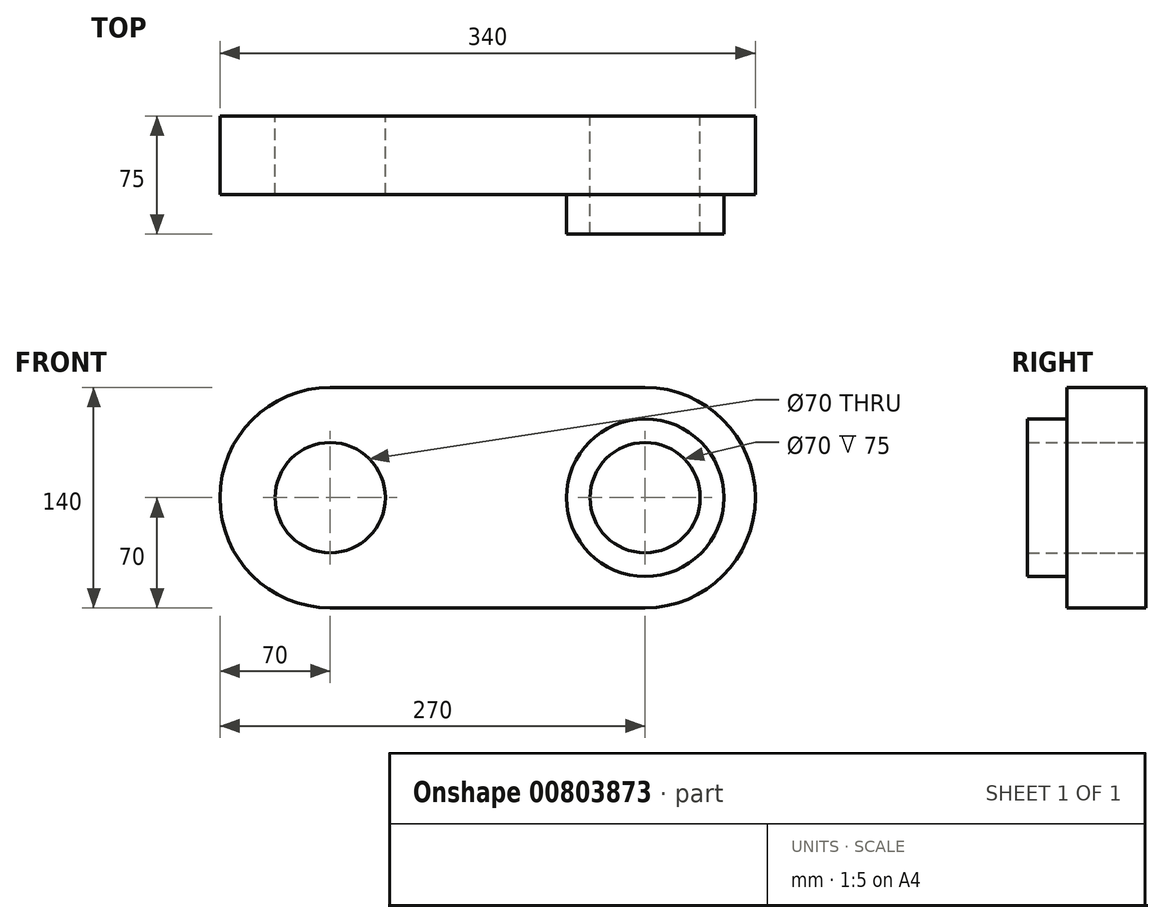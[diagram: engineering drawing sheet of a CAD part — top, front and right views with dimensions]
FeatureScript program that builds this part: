
annotation { "Feature Type Name" : "Feature", "Feature Type Description" : "" }
export const myFeature = defineFeature(function(context is Context, id is Id, definition is map)
    precondition{}
    {
        {
            var Q0;
            Q0=qCreatedBy(makeId("Front.planeOp"),FACE);
            var sketch = newSketch(context, id + "F0", { "sketchPlane" : qUnion([Q0])});
            skLineSegment(sketch, "E0.bottom", {"start": v(-100, 70) * mm, "end": v(100, 70) * mm});
            skLineSegment(sketch, "E0.top", {"start": v(-100, -70) * mm, "end": v(100, -70) * mm});
            skLineSegment(sketch, "E0.left", {"start": v(-100, 70) * mm, "end": v(-100, -70) * mm, "construction": true});
            skLineSegment(sketch, "E0.right", {"start": v(100, 70) * mm, "end": v(100, -70) * mm, "construction": true});
            skLineSegment(sketch, "E1", {"start": v(-100, 0) * mm, "end": v(100, 0) * mm, "construction": true});
            skCircle(sketch, "E2", {"center": v(-100, 0) * mm, "radius": 35 * mm});
            skArc(sketch, "E3", {"start": v(-100, 70) * mm, "mid": v(-170, 0) * mm, "end": v(-100, -70) * mm});
            skCircle(sketch, "E4", {"center": v(100, 0) * mm, "radius": 35 * mm});
            skArc(sketch, "E5", {"start": v(100, -70) * mm, "mid": v(170, 0) * mm, "end": v(100, 70) * mm});
            skSolve(sketch);
        }
        {
            var Q0;
            Q0=makeQuery(id+"F0.imprint","IMPRINT",FACE,{"disambiguationData":[TD([[makeQuery(id+"F0.imprint","IMPRINT",EDGE,{"derivedFrom":sQuery(id+"F0.wireOp",EDGE,"E0.bottom")}),-1.0]])]});
            extrude(context, id + "F1", {"entities" : qUnion([Q0]), "endBound" : BoundingType.SYMMETRIC, "depth" : 50 * mm, "offsetDistance" : 25 * mm});
        }
        {
            var Q0;
            Q0=makeQuery(id+"F1.opExtrude","CAP_FACE",FACE,{"disambiguationData":[OSD([sQuery(id+"F0.wireOp",EDGE,"E0.bottom"),sQuery(id+"F0.wireOp",EDGE,"E0.top"),sQuery(id+"F0.wireOp",EDGE,"E2"),sQuery(id+"F0.wireOp",EDGE,"E3"),sQuery(id+"F0.wireOp",EDGE,"E4"),sQuery(id+"F0.wireOp",EDGE,"E5")])],"isStart":false});
            var sketch = newSketch(context, id + "F2", { "sketchPlane" : qUnion([Q0])});
            skCircle(sketch, "E6.0", {"center": v(100, 0) * mm, "radius": 35 * mm});
            skCircle(sketch, "E7", {"center": v(100, 0) * mm, "radius": 50 * mm});
            skSolve(sketch);
        }
        {
            var Q0;
            Q0 = qSketchRegion(id + "F2", true);
            extrude(context, id + "F3", {"entities" : qUnion([Q0]), "operationType" : NewBodyOperationType.ADD, "depth" : 25 * mm, "offsetDistance" : 25 * mm});
        }
    });
